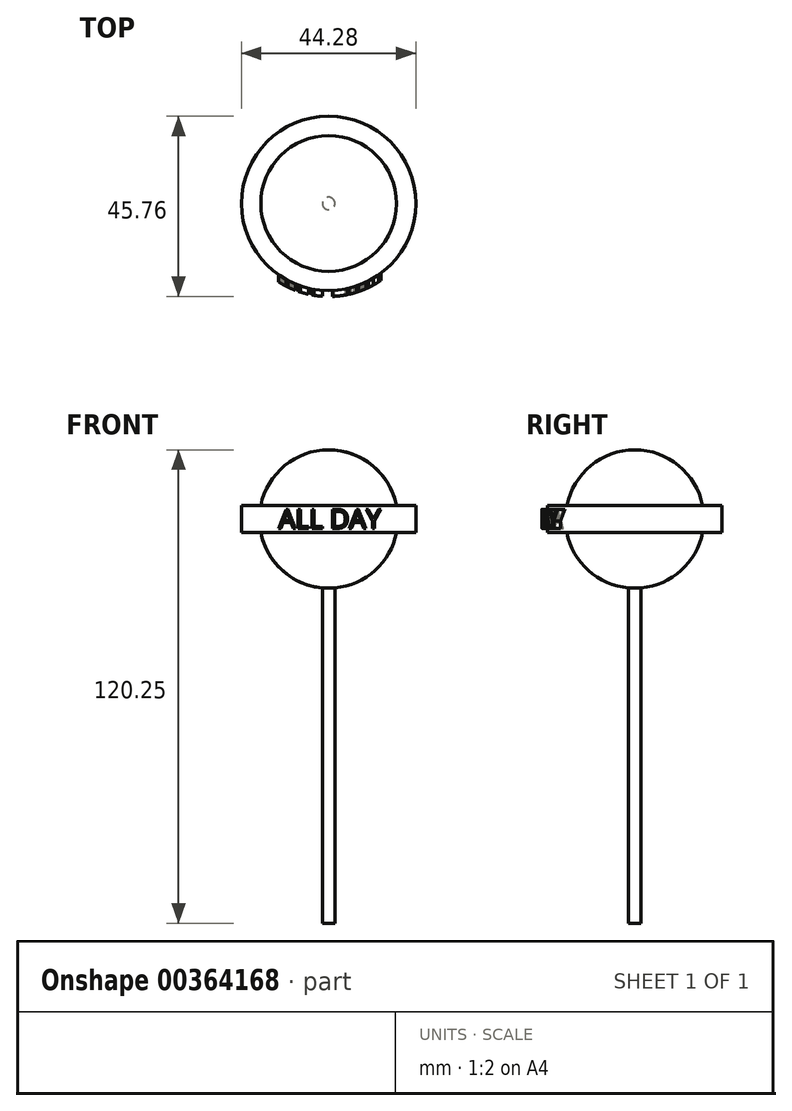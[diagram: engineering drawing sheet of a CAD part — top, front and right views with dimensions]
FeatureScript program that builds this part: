
annotation { "Feature Type Name" : "Feature", "Feature Type Description" : "" }
export const myFeature = defineFeature(function(context is Context, id is Id, definition is map)
    precondition{}
    {
        {
            var Q0;
            Q0=qCreatedBy(makeId("Front.planeOp"),FACE);
            var sketch = newSketch(context, id + "F0", { "sketchPlane" : qUnion([Q0])});
            skArc(sketch, "E0", {"start": v(0, -17.57) * mm, "mid": v(17.57, 0) * mm, "end": v(0, 17.57) * mm});
            skLineSegment(sketch, "E1", {"start": v(0, 17.57) * mm, "end": v(0, -17.57) * mm});
            skLineSegment(sketch, "E2", {"start": v(0, 0) * mm, "end": v(0, 54.82) * mm, "construction": true});
            skLineSegment(sketch, "E3.bottom", {"start": v(22.14, 3.4) * mm, "end": v(7.86, 3.4) * mm});
            skLineSegment(sketch, "E3.top", {"start": v(22.14, -3.4) * mm, "end": v(7.86, -3.4) * mm});
            skLineSegment(sketch, "E3.left", {"start": v(22.14, 3.4) * mm, "end": v(22.14, -3.4) * mm});
            skLineSegment(sketch, "E3.right", {"start": v(7.86, 3.4) * mm, "end": v(7.86, -3.4) * mm});
            skPoint(sketch, "E3.middle", {"position": v(15, 0) * mm});
            skLineSegment(sketch, "E4.bottom", {"start": v(0, -15) * mm, "end": v(1.6, -15) * mm});
            skLineSegment(sketch, "E4.top", {"start": v(0, -102.68) * mm, "end": v(1.6, -102.68) * mm});
            skLineSegment(sketch, "E4.left", {"start": v(0, -15) * mm, "end": v(0, -102.68) * mm});
            skLineSegment(sketch, "E4.right", {"start": v(1.6, -15) * mm, "end": v(1.6, -102.68) * mm});
            skSolve(sketch);
        }
        {
            var Q0;
            Q0 = qSketchRegion(id + "F0", true);
            var Q1;
            Q1=sQuery(id+"F0.wireOp",EDGE,"E2");
            revolve(context, id + "F1", {"entities" : qUnion([Q0]), "axis" : qUnion([Q1]), "revolveType" : RevolveType.FULL});
        }
        {
            var Q0;
            Q0=qCreatedBy(makeId("Front.planeOp"),FACE);
            var sketch = newSketch(context, id + "F2", { "sketchPlane" : qUnion([Q0])});
            skText(sketch, "E5", { "text": "ALL DAY", "fontName": "OpenSans-Regular.ttf"});
            const initialGuessF2  = {"E5": [-0.0127, -0.00236, 1, 0, 0.00485]};
            skSetInitialGuess(sketch, initialGuessF2);
            skSolve(sketch);
        }
        {
            var Q0;
            Q0 = qSketchRegion(id + "F2", true);
            extrude(context, id + "F3", {"entities" : qUnion([Q0]), "operationType" : NewBodyOperationType.ADD, "depth" : 28.5 * mm});
        }
        {
            var Q0;
            Q0=qCreatedBy(makeId("Front.planeOp"),FACE);
            var sketch = newSketch(context, id + "F4", { "sketchPlane" : qUnion([Q0])});
            skLineSegment(sketch, "E6", {"start": v(22.14, 3.4) * mm, "end": v(22.14, -3.4) * mm});
            skLineSegment(sketch, "E7", {"start": v(0, 0) * mm, "end": v(0, 59.77) * mm, "construction": true});
            skLineSegment(sketch, "E8.0", {"start": v(23.64, -4.9) * mm, "end": v(18.05, -4.9) * mm});
            skLineSegment(sketch, "E8.1", {"start": v(23.64, 4.9) * mm, "end": v(23.64, -4.9) * mm});
            skLineSegment(sketch, "E8.2", {"start": v(23.64, 4.9) * mm, "end": v(17.6, 4.9) * mm});
            skLineSegment(sketch, "E9", {"start": v(17.6, 4.9) * mm, "end": v(15.2, 12.47) * mm});
            skLineSegment(sketch, "E10", {"start": v(15.2, 12.47) * mm, "end": v(29.12, 12.77) * mm});
            skLineSegment(sketch, "E11", {"start": v(29.12, 12.77) * mm, "end": v(34.47, 0.98) * mm});
            skLineSegment(sketch, "E12", {"start": v(34.47, 0.98) * mm, "end": v(34.47, -11.88) * mm});
            skLineSegment(sketch, "E13", {"start": v(34.47, -11.88) * mm, "end": v(19.1, -15.32) * mm});
            skLineSegment(sketch, "E14", {"start": v(19.1, -15.32) * mm, "end": v(18.05, -4.9) * mm});
            skSolve(sketch);
        }
        {
            var Q0;
            Q0 = qSketchRegion(id + "F4", true);
            var Q1;
            Q1=sQuery(id+"F4.wireOp",EDGE,"E7");
            revolve(context, id + "F5", {"operationType" : NewBodyOperationType.REMOVE, "entities" : qUnion([Q0]), "axis" : qUnion([Q1]), "revolveType" : RevolveType.FULL, "oppositeDirection" : true});
        }
    });
